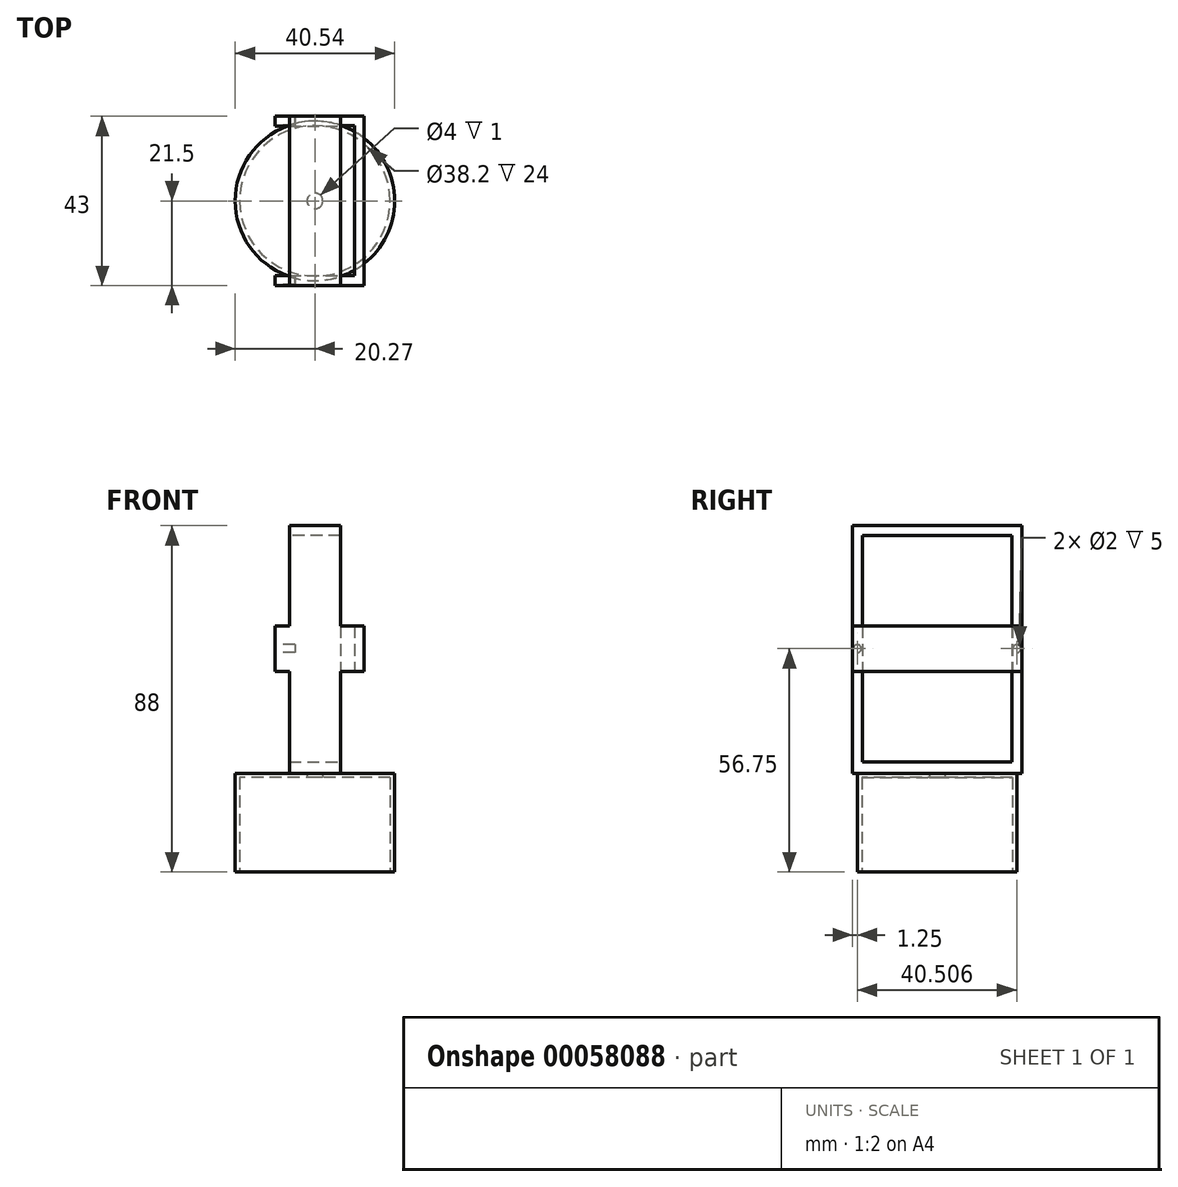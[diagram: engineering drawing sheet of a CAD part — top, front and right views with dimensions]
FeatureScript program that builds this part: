
annotation { "Feature Type Name" : "Feature", "Feature Type Description" : "" }
export const myFeature = defineFeature(function(context is Context, id is Id, definition is map)
    precondition{}
    {
        {
            var Q0;
            Q0=qCreatedBy(makeId("Top.planeOp"),FACE);
            var sketch = newSketch(context, id + "F0", { "sketchPlane" : qUnion([Q0])});
            skCircle(sketch, "E0", {"center": v(0, 0) * mm, "radius": 19.1 * mm});
            skCircle(sketch, "E1", {"center": v(0, 0) * mm, "radius": 20.27 * mm});
            skCircle(sketch, "E2", {"center": v(0, 0) * mm, "radius": 2 * mm});
            skSolve(sketch);
        }
        {
            var Q0;
            Q0=makeQuery(id+"F0.imprint","IMPRINT",FACE,{"disambiguationData":[TD([[makeQuery(id+"F0.imprint","IMPRINT",EDGE,{"derivedFrom":sQuery(id+"F0.wireOp",EDGE,"E0")}),-1.0]])]});
            var Q1;
            Q1=makeQuery(id+"F0.imprint","IMPRINT",FACE,{"disambiguationData":[TD([[makeQuery(id+"F0.imprint","IMPRINT",EDGE,{"derivedFrom":sQuery(id+"F0.wireOp",EDGE,"E0")}),1.0]])]});
            extrude(context, id + "F1", {"entities" : qUnion([Q0, Q1]), "depth" : 25 * mm});
        }
        {
            var Q0;
            Q0=makeQuery(id+"F0.imprint","IMPRINT",FACE,{"disambiguationData":[TD([[makeQuery(id+"F0.imprint","IMPRINT",EDGE,{"derivedFrom":sQuery(id+"F0.wireOp",EDGE,"E0")}),1.0]])]});
            extrude(context, id + "F2", {"entities" : qUnion([Q0]), "operationType" : NewBodyOperationType.REMOVE, "depth" : 24 * mm});
        }
        {
            var Q0;
            Q0=makeQuery(id+"F1.opExtrude","CAP_FACE",FACE,{"disambiguationData":[OSD([sQuery(id+"F0.wireOp",EDGE,"E1"),sQuery(id+"F0.wireOp",EDGE,"E2")])],"isStart":false});
            var sketch = newSketch(context, id + "F3", { "sketchPlane" : qUnion([Q0])});
            skLineSegment(sketch, "E3.rect.bottom", {"start": v(6.5, -6.5) * mm, "end": v(-6.5, -6.5) * mm});
            skLineSegment(sketch, "E3.rect.top", {"start": v(6.5, 6.5) * mm, "end": v(-6.5, 6.5) * mm});
            skLineSegment(sketch, "E3.rect.left", {"start": v(6.5, -6.5) * mm, "end": v(6.5, 6.5) * mm});
            skLineSegment(sketch, "E3.rect.right", {"start": v(-6.5, -6.5) * mm, "end": v(-6.5, 6.5) * mm});
            skPoint(sketch, "E3.rect.middle", {"position": v(0, 0) * mm});
            skSolve(sketch);
        }
        {
            var Q0;
            Q0 = qSketchRegion(id + "F3", true);
            var Q1;
            Q1=makeQuery(id+"F3.imprint","IMPRINT",FACE,{"disambiguationData":[TD([[makeQuery(id+"F3.imprint","IMPRINT",EDGE,{"derivedFrom":sQuery(id+"F3.wireOp",EDGE,"E3.rect.bottom")}),-1.0]])]});
            extrude(context, id + "F4", {"entities" : qUnion([Q0, Q1]), "operationType" : NewBodyOperationType.ADD, "depth" : 3 * mm});
        }
        {
            var Q0;
            Q0=makeQuery(id+"F4.opExtrude","SWEPT_FACE",FACE,{"disambiguationData":[OSD([sQuery(id+"F3.wireOp",EDGE,"E3.rect.bottom")])]});
            extrude(context, id + "F5", {"entities" : qUnion([Q0]), "operationType" : NewBodyOperationType.ADD, "depth" : 15 * mm});
        }
        {
            var Q0;
            Q0=makeQuery(id+"F4.opExtrude","SWEPT_FACE",FACE,{"disambiguationData":[OSD([sQuery(id+"F3.wireOp",EDGE,"E3.rect.top")])]});
            extrude(context, id + "F6", {"entities" : qUnion([Q0]), "operationType" : NewBodyOperationType.ADD, "depth" : 15 * mm});
        }
        {
            var Q0;
            {var subQ0=sQuery(id+"F3.wireOp",EDGE,"E3.rect.top");var subQ1=sQuery(id+"F3.wireOp",EDGE,"E3.rect.bottom");Q0=makeQuery(id+"F6.boolean.opBoolean","MERGE",FACE,{"derivedFrom":[makeQuery(id+"F5.boolean.opBoolean","MERGE",FACE,{"derivedFrom":[makeQuery(id+"F4.opExtrude","CAP_FACE",FACE,{"disambiguationData":[OSD([subQ1,subQ0,sQuery(id+"F3.wireOp",EDGE,"E3.rect.left"),sQuery(id+"F3.wireOp",EDGE,"E3.rect.right")])],"isStart":false}),makeQuery(id+"F5.opExtrude","SWEPT_FACE",FACE,{"disambiguationData":[OSD([subQ1]),TDD([makeQuery(id+"F4.opExtrude","CAP_EDGE",EDGE,{"disambiguationData":[OSD([subQ1])],"isStart":false})])]})]}),makeQuery(id+"F6.opExtrude","SWEPT_FACE",FACE,{"disambiguationData":[OSD([subQ0]),TDD([makeQuery(id+"F4.opExtrude","CAP_EDGE",EDGE,{"disambiguationData":[OSD([subQ0])],"isStart":false})])]})]});}
            var sketch = newSketch(context, id + "F7", { "sketchPlane" : qUnion([Q0])});
            skLineSegment(sketch, "E4.bottom", {"start": v(-6.5, -21.5) * mm, "end": v(6.5, -21.5) * mm});
            skLineSegment(sketch, "E4.top", {"start": v(-6.5, -19) * mm, "end": v(6.5, -19) * mm});
            skLineSegment(sketch, "E4.left", {"start": v(-6.5, -21.5) * mm, "end": v(-6.5, -19) * mm});
            skLineSegment(sketch, "E4.right", {"start": v(6.5, -21.5) * mm, "end": v(6.5, -19) * mm});
            skLineSegment(sketch, "E5.bottom", {"start": v(-6.5, 21.5) * mm, "end": v(6.5, 21.5) * mm});
            skLineSegment(sketch, "E5.top", {"start": v(-6.5, 19) * mm, "end": v(6.5, 19) * mm});
            skLineSegment(sketch, "E5.left", {"start": v(-6.5, 21.5) * mm, "end": v(-6.5, 19) * mm});
            skLineSegment(sketch, "E5.right", {"start": v(6.5, 21.5) * mm, "end": v(6.5, 19) * mm});
            skSolve(sketch);
        }
        {
            var Q0;
            Q0 = qSketchRegion(id + "F7", true);
            var Q1;
            Q1=makeQuery(id+"F7.imprint","IMPRINT",FACE,{"disambiguationData":[TD([[makeQuery(id+"F7.imprint","IMPRINT",EDGE,{"derivedFrom":sQuery(id+"F7.wireOp",EDGE,"E4.bottom")}),-1.0]])]});
            extrude(context, id + "F8", {"entities" : qUnion([Q0, Q1]), "operationType" : NewBodyOperationType.ADD, "depth" : 60 * mm});
        }
        {
            var Q0;
            Q0=makeQuery(id+"F8.opExtrude","SWEPT_FACE",FACE,{"disambiguationData":[OSD([sQuery(id+"F7.wireOp",EDGE,"E5.top")])]});
            var sketch = newSketch(context, id + "F9", { "sketchPlane" : qUnion([Q0])});
            skLineSegment(sketch, "E6.bottom", {"start": v(6.5, 88) * mm, "end": v(-6.5, 88) * mm});
            skLineSegment(sketch, "E6.top", {"start": v(6.5, 85.5) * mm, "end": v(-6.5, 85.5) * mm});
            skLineSegment(sketch, "E6.left", {"start": v(6.5, 88) * mm, "end": v(6.5, 85.5) * mm});
            skLineSegment(sketch, "E6.right", {"start": v(-6.5, 88) * mm, "end": v(-6.5, 85.5) * mm});
            skSolve(sketch);
        }
        {
            var Q0;
            Q0 = qSketchRegion(id + "F9", true);
            var Q1;
            Q1=makeQuery(id+"F9.imprint","IMPRINT",FACE,{"disambiguationData":[TD([[makeQuery(id+"F9.imprint","IMPRINT",EDGE,{"derivedFrom":sQuery(id+"F9.wireOp",EDGE,"E6.bottom")}),-1.0]])]});
            extrude(context, id + "F10", {"entities" : qUnion([Q0, Q1]), "operationType" : NewBodyOperationType.ADD, "depth" : 40 * mm});
        }
        {
            var Q0;
            {var subQ0=sQuery(id+"F3.wireOp",EDGE,"E3.rect.left");Q0=makeQuery(id+"F10.boolean.opBoolean","MERGE",FACE,{"derivedFrom":[makeQuery(id+"F8.boolean.opBoolean","MERGE",FACE,{"derivedFrom":[makeQuery(id+"F6.boolean.opBoolean","MERGE",FACE,{"derivedFrom":[makeQuery(id+"F5.boolean.opBoolean","MERGE",FACE,{"derivedFrom":[makeQuery(id+"F4.opExtrude","SWEPT_FACE",FACE,{"disambiguationData":[OSD([subQ0])]}),makeQuery(id+"F5.opExtrude","SWEPT_FACE",FACE,{"disambiguationData":[OSD([sQuery(id+"F3.wireOp",EDGE,"E3.rect.bottom"),subQ0])]})]}),makeQuery(id+"F6.opExtrude","SWEPT_FACE",FACE,{"disambiguationData":[OSD([sQuery(id+"F3.wireOp",EDGE,"E3.rect.top"),subQ0])]})]}),makeQuery(id+"F8.opExtrude","SWEPT_FACE",FACE,{"disambiguationData":[OSD([sQuery(id+"F7.wireOp",EDGE,"E4.right")])]}),makeQuery(id+"F8.opExtrude","SWEPT_FACE",FACE,{"disambiguationData":[OSD([sQuery(id+"F7.wireOp",EDGE,"E5.right")])]})]}),makeQuery(id+"F10.opExtrude","SWEPT_FACE",FACE,{"disambiguationData":[OSD([sQuery(id+"F9.wireOp",EDGE,"E6.left")])]})]});}
            var sketch = newSketch(context, id + "F11", { "sketchPlane" : qUnion([Q0])});
            skLineSegment(sketch, "E7.bottom", {"start": v(-21.5, 62.5) * mm, "end": v(-19, 62.5) * mm});
            skLineSegment(sketch, "E7.top", {"start": v(-21.5, 51) * mm, "end": v(-19, 51) * mm});
            skLineSegment(sketch, "E7.left", {"start": v(-21.5, 62.5) * mm, "end": v(-21.5, 51) * mm});
            skLineSegment(sketch, "E7.right", {"start": v(-19, 62.5) * mm, "end": v(-19, 51) * mm});
            skLineSegment(sketch, "E8.bottom", {"start": v(19.18, 62.5) * mm, "end": v(21.68, 62.5) * mm});
            skLineSegment(sketch, "E8.top", {"start": v(19.18, 51) * mm, "end": v(21.68, 51) * mm});
            skLineSegment(sketch, "E8.left", {"start": v(19.18, 62.5) * mm, "end": v(19.18, 51) * mm});
            skLineSegment(sketch, "E8.right", {"start": v(21.68, 62.5) * mm, "end": v(21.68, 51) * mm});
            skSolve(sketch);
        }
        {
            var Q0;
            Q0=makeQuery(id+"F11.imprint","IMPRINT",FACE,{"disambiguationData":[TD([[makeQuery(id+"F11.imprint","IMPRINT",EDGE,{"derivedFrom":sQuery(id+"F11.wireOp",EDGE,"E7.bottom")}),-1.0]])]});
            var Q1;
            {var subQ0=sQuery(id+"F11.wireOp",EDGE,"E8.left");Q1=makeQuery(id+"F11.imprint","IMPRINT",FACE,{"disambiguationData":[TD([[makeQuery(id+"F11.imprint","IMPRINT",EDGE,{"derivedFrom":subQ0}),1.0]])]});}
            extrude(context, id + "F12", {"entities" : qUnion([Q0, Q1]), "operationType" : NewBodyOperationType.ADD, "depth" : 6 * mm});
        }
        {
            var Q0;
            Q0=makeQuery(id+"F12.boolean.opBoolean","MERGE",FACE,{"derivedFrom":[makeQuery(id+"F8.opExtrude","SWEPT_FACE",FACE,{"disambiguationData":[OSD([sQuery(id+"F7.wireOp",EDGE,"E4.top")])]}),makeQuery(id+"F12.opExtrude","SWEPT_FACE",FACE,{"disambiguationData":[OSD([sQuery(id+"F11.wireOp",EDGE,"E7.right")])]})]});
            var sketch = newSketch(context, id + "F13", { "sketchPlane" : qUnion([Q0])});
            skLineSegment(sketch, "E9.bottom", {"start": v(-12.5, 62.5) * mm, "end": v(-10, 62.5) * mm});
            skLineSegment(sketch, "E9.top", {"start": v(-12.5, 51) * mm, "end": v(-10, 51) * mm});
            skLineSegment(sketch, "E9.left", {"start": v(-12.5, 62.5) * mm, "end": v(-12.5, 51) * mm});
            skLineSegment(sketch, "E9.right", {"start": v(-10, 62.5) * mm, "end": v(-10, 51) * mm});
            skSolve(sketch);
        }
        {
            var Q0;
            Q0=makeQuery(id+"F13.imprint","IMPRINT",FACE,{"disambiguationData":[TD([[makeQuery(id+"F13.imprint","IMPRINT",EDGE,{"derivedFrom":sQuery(id+"F13.wireOp",EDGE,"E9.bottom")}),-1.0]])]});
            extrude(context, id + "F14", {"entities" : qUnion([Q0]), "operationType" : NewBodyOperationType.ADD, "depth" : 40 * mm});
        }
        {
            var Q0;
            {var subQ0=sQuery(id+"F3.wireOp",EDGE,"E3.rect.right");Q0=makeQuery(id+"F10.boolean.opBoolean","MERGE",FACE,{"derivedFrom":[makeQuery(id+"F8.boolean.opBoolean","MERGE",FACE,{"derivedFrom":[makeQuery(id+"F6.boolean.opBoolean","MERGE",FACE,{"derivedFrom":[makeQuery(id+"F5.boolean.opBoolean","MERGE",FACE,{"derivedFrom":[makeQuery(id+"F4.opExtrude","SWEPT_FACE",FACE,{"disambiguationData":[OSD([subQ0])]}),makeQuery(id+"F5.opExtrude","SWEPT_FACE",FACE,{"disambiguationData":[OSD([sQuery(id+"F3.wireOp",EDGE,"E3.rect.bottom"),subQ0])]})]}),makeQuery(id+"F6.opExtrude","SWEPT_FACE",FACE,{"disambiguationData":[OSD([sQuery(id+"F3.wireOp",EDGE,"E3.rect.top"),subQ0])]})]}),makeQuery(id+"F8.opExtrude","SWEPT_FACE",FACE,{"disambiguationData":[OSD([sQuery(id+"F7.wireOp",EDGE,"E4.left")])]}),makeQuery(id+"F8.opExtrude","SWEPT_FACE",FACE,{"disambiguationData":[OSD([sQuery(id+"F7.wireOp",EDGE,"E5.left")])]})]}),makeQuery(id+"F10.opExtrude","SWEPT_FACE",FACE,{"disambiguationData":[OSD([sQuery(id+"F9.wireOp",EDGE,"E6.right")])]})]});}
            var sketch = newSketch(context, id + "F15", { "sketchPlane" : qUnion([Q0])});
            skLineSegment(sketch, "E10.bottom", {"start": v(-19, 62.5) * mm, "end": v(-21.5, 62.5) * mm});
            skLineSegment(sketch, "E10.top", {"start": v(-19, 51) * mm, "end": v(-21.5, 51) * mm});
            skLineSegment(sketch, "E10.left", {"start": v(-19, 62.5) * mm, "end": v(-19, 51) * mm});
            skLineSegment(sketch, "E10.right", {"start": v(-21.5, 62.5) * mm, "end": v(-21.5, 51) * mm});
            skLineSegment(sketch, "E11.bottom", {"start": v(21.5, 62.5) * mm, "end": v(19, 62.5) * mm});
            skLineSegment(sketch, "E11.top", {"start": v(21.5, 51) * mm, "end": v(19, 51) * mm});
            skLineSegment(sketch, "E11.left", {"start": v(21.5, 62.5) * mm, "end": v(21.5, 51) * mm});
            skLineSegment(sketch, "E11.right", {"start": v(19, 62.5) * mm, "end": v(19, 51) * mm});
            skSolve(sketch);
        }
        {
            var Q0;
            Q0=makeQuery(id+"F15.imprint","IMPRINT",FACE,{"disambiguationData":[TD([[makeQuery(id+"F15.imprint","IMPRINT",EDGE,{"derivedFrom":sQuery(id+"F15.wireOp",EDGE,"E11.bottom")}),1.0]])]});
            var Q1;
            Q1=makeQuery(id+"F15.imprint","IMPRINT",FACE,{"disambiguationData":[TD([[makeQuery(id+"F15.imprint","IMPRINT",EDGE,{"derivedFrom":sQuery(id+"F15.wireOp",EDGE,"E10.bottom")}),1.0]])]});
            extrude(context, id + "F16", {"entities" : qUnion([Q0, Q1]), "operationType" : NewBodyOperationType.ADD, "depth" : 3.6 * mm});
        }
        {
            var Q0;
            Q0=makeQuery(id+"F16.opExtrude","CAP_FACE",FACE,{"disambiguationData":[OSD([sQuery(id+"F15.wireOp",EDGE,"E10.bottom"),sQuery(id+"F15.wireOp",EDGE,"E10.top"),sQuery(id+"F15.wireOp",EDGE,"E10.left"),sQuery(id+"F15.wireOp",EDGE,"E10.right")])],"isStart":false});
            var sketch = newSketch(context, id + "F17", { "sketchPlane" : qUnion([Q0])});
            skCircle(sketch, "E12", {"center": v(-20.26, 56.75) * mm, "radius": 1 * mm});
            skSolve(sketch);
        }
        {
            var Q0;
            Q0=makeQuery(id+"F16.opExtrude","CAP_FACE",FACE,{"disambiguationData":[OSD([sQuery(id+"F15.wireOp",EDGE,"E11.bottom"),sQuery(id+"F15.wireOp",EDGE,"E11.top"),sQuery(id+"F15.wireOp",EDGE,"E11.left"),sQuery(id+"F15.wireOp",EDGE,"E11.right")])],"isStart":false});
            var sketch = newSketch(context, id + "F18", { "sketchPlane" : qUnion([Q0])});
            skCircle(sketch, "E13", {"center": v(20.25, 56.75) * mm, "radius": 1 * mm});
            skSolve(sketch);
        }
        {
            var Q0;
            Q0 = qSketchRegion(id + "F18", true);
            var Q1;
            Q1=makeQuery(id+"F17.imprint","IMPRINT",FACE,{"disambiguationData":[TD([[makeQuery(id+"F17.imprint","IMPRINT",EDGE,{"derivedFrom":sQuery(id+"F17.wireOp",EDGE,"E12")}),1.0]])]});
            extrude(context, id + "F19", {"entities" : qUnion([Q0, Q1]), "operationType" : NewBodyOperationType.REMOVE, "oppositeDirection" : true, "depth" : 5 * mm});
        }
    });
